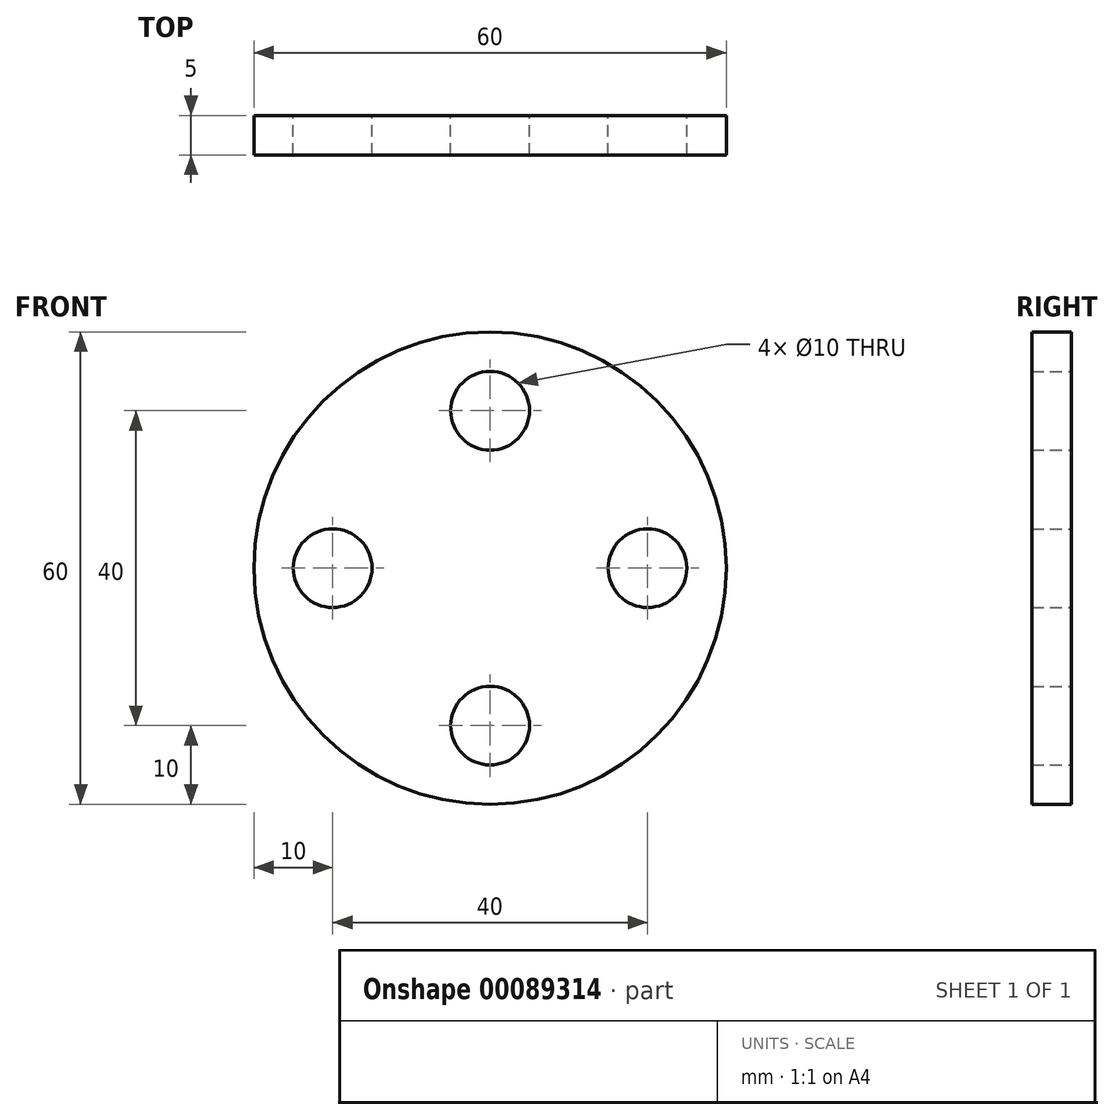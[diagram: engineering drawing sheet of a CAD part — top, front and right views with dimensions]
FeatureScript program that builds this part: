
annotation { "Feature Type Name" : "Feature", "Feature Type Description" : "" }
export const myFeature = defineFeature(function(context is Context, id is Id, definition is map)
    precondition{}
    {
        {
            var Q0;
            Q0=qCreatedBy(makeId("Front.planeOp"),FACE);
            var sketch = newSketch(context, id + "F0", { "sketchPlane" : qUnion([Q0])});
            skCircle(sketch, "E0", {"center": v(0, 0) * mm, "radius": 30 * mm});
            skCircle(sketch, "E1", {"center": v(0, 0) * mm, "radius": 20 * mm, "construction": true});
            skCircle(sketch, "E2", {"center": v(0, 20) * mm, "radius": 5 * mm});
            skCircle(sketch, "E3", {"center": v(20, 0) * mm, "radius": 5 * mm});
            skCircle(sketch, "E4", {"center": v(0, -20) * mm, "radius": 5 * mm});
            skCircle(sketch, "E5", {"center": v(-20, 0) * mm, "radius": 5 * mm});
            skSolve(sketch);
        }
        {
            var Q0;
            Q0 = qSketchRegion(id + "F0", true);
            extrude(context, id + "F1", {"entities" : qUnion([Q0]), "depth" : 5 * mm});
        }
    });
